# Revit family: ПТУ_отдельный фундамент
name_source: partatom
category: Специальное оборудование
units: mm (PartAtom-declared; Revit-internal decimal feet)

## family parameters
Всегда вертикально = Нет
На основе рабочей плоскости = Нет
Общий = Нет
При загрузке вырезать с полостями = Нет
Размер круглого соединителя = Использовать диаметр
Тип детали = Нормальный
Точка расчета площади = Нет

## types (8) — shared parameters
ADSK_Единица измерения = шт.
ADSK_Завод-изготовитель = FENSYS
ADSK_Комплект = ПТУ
URL = https://www.fensys.ru
Объём бетона = 8.5
Объём вынимаего грунта = 8.6

## per-type parameters (varying)
| type | ADSK_Код изделия | ADSK_Масса | ADSK_Наименование | ADSK_Обозначение | Длина стрелы |
| ПТУ с раздельными фундаментами., под 6000.,Тёплое исполнение | 53415 | 2700 | Противотаранное устройство с вертикальным подъемом стрелы для остановки т/с массой 3,5 т на скорости 40 км/ч. Перекрываемый проезд 6 м. Электромеханический привод. В комплекте с фундаментом  - армокаркас под бетонирование. Высота стрелы над дорогой - 860 мм. Время закрывания 12 с. Потр. мощность 3 кВт. Температура эксплуатации -20°-+50°. В комплекте: ШУ, пост управления, ф/э безопасности, маячок. | ПТУ-Л 6000ТА | 6000 мм |
| ПТУ с раздельными фундаментами., под 6000.,Холодное исполнение | 53407 | 2700 | Противотаранное устройство с вертикальным подъемом стрелы для остановки т/с массой 3,5 т на скорости 40 км/ч. Перекрываемый проезд 6 м. Электромеханический привод. В комплекте с фундаментом  - армокаркас под бетонирование. Высота стрелы над дорогой - 860 мм. Время закрывания 12 с. Потр.мощность 5 кВт. Температура эксплуатации -55°-+50°. В комплекте: ШУ, пост управления, ф/э безопасности, маячок. | ПТУ-Л 6000ХА | 6000 мм |
| ПТУ с раздельными фундаментами., под 4000.,Тёплое исполнение | 53412 | 2450 | Противотаранное устройство с вертикальным подъемом стрелы для остановки т/с массой 3,5 т на скорости 40 км/ч. Перекрываемый проезд 4 м. Электромеханический привод. В комплекте с фундаментом - армокаркас под бетонирование. Высота стрелы над дорогой - 860 мм. Время закрывания 12 с. Потр. мощность 3 кВт. Температура эксплуатации -20°-+50°. В комплекте: ШУ, пост управления, ф/э безопасности, маячок. | ПТУ-Л 4000ТА | 4000 мм |
| ПТУ с раздельными фундаментами., под 4000.,Холодное исполнение | 53404 | 2450 | Противотаранное устройство с вертикальным подъемом стрелы для остановки т/с массой 3,5 т на скорости 40 км/ч. Перекрываемый проезд 4 м. Электромеханический привод. В комплекте с фундаментом - армокаркас под бетонирование. Высота стрелы над дорогой - 860 мм. Время закрывания 12 с. Потр.мощность 5 кВт. Температура эксплуатации -55°-+50°. В комплекте: ШУ, пост управления, ф/э безопасности, маячок. | ПТУ-Л 4000ХА | 4000 мм |
| ПТУ с раздельными фундаментами., под 4500.,Тёплое исполнение | 53413 | 2500 | Противотаранное устройство с вертикальным подъемом стрелы для остановки т/с массой 3,5 т на скорости 40 км/ч. Перекрываемый проезд 4,5 м. Электромеханический привод. В комплекте с фундаментом - армокаркас под бетонирование. Высота стрелы над дорогой - 860 мм. Время закрывания 12 с. Потр. мощность 3 кВт. Температура эксплуатации -20°-+50°. В комплекте: ШУ, пост управления, ф/э безопасности, маячок. | ПТУ-Л 4500ТА | 4500 мм |
| ПТУ с раздельными фундаментами., под 4500.,Холодное исполнение | 53405 | 2500 | Противотаранное устройство с вертикальным подъемом стрелы для остановки т/с массой 3,5 т на скорости 40 км/ч. Перекрываемый проезд 4,5 м. Электромеханический привод. В комплекте с фундаментом - армокаркас под бетонирование. Высота стрелы над дорогой - 860 мм. Время закрывания 12 с. Потр.мощность 5 кВт. Температура эксплуатации -55°-+50°. В комплекте: ШУ, пост управления, ф/э безопасности, маячок. | ПТУ-Л 4500ХА | 4500 мм |
| ПТУ с раздельными фундаментами., под 5000.,Холодное исполнение | 53406 | 2550 | Противотаранное устройство с вертикальным подъемом стрелы для остановки т/с массой 3,5 т на скорости 40 км/ч. Перекрываемый проезд 5 м. Электромеханический привод. В комплекте с фундаментом  - армокаркас под бетонирование. Высота стрелы над дорогой - 860 мм. Время закрывания 12 с. Потр.мощность 5 кВт. Температура эксплуатации -55°-+50°. В комплекте: ШУ, пост управления,ф/э безопасности, маячок. | ПТУ-Л 5000ХА | 5000 мм |
| ПТУ с раздельными фундаментами., под 5000.,Тёплое исполнение | 53414 | 2550 | Противотаранное устройство с вертикальным подъемом стрелы для остановки т/с массой 3,5 т на скорости 40 км/ч. Перекрываемый проезд 5 м. Электромеханический привод. В комплекте с фундаментом  - армокаркас под бетонирование. Высота стрелы над дорогой - 860 мм. Время закрывания 12 с. Потр. мощность 3 кВт. Температура эксплуатации -20°-+50°. В комплекте: ШУ, пост управления,ф/э безопасности, маячок. | ПТУ-Л 5000ТА | 5000 мм |
